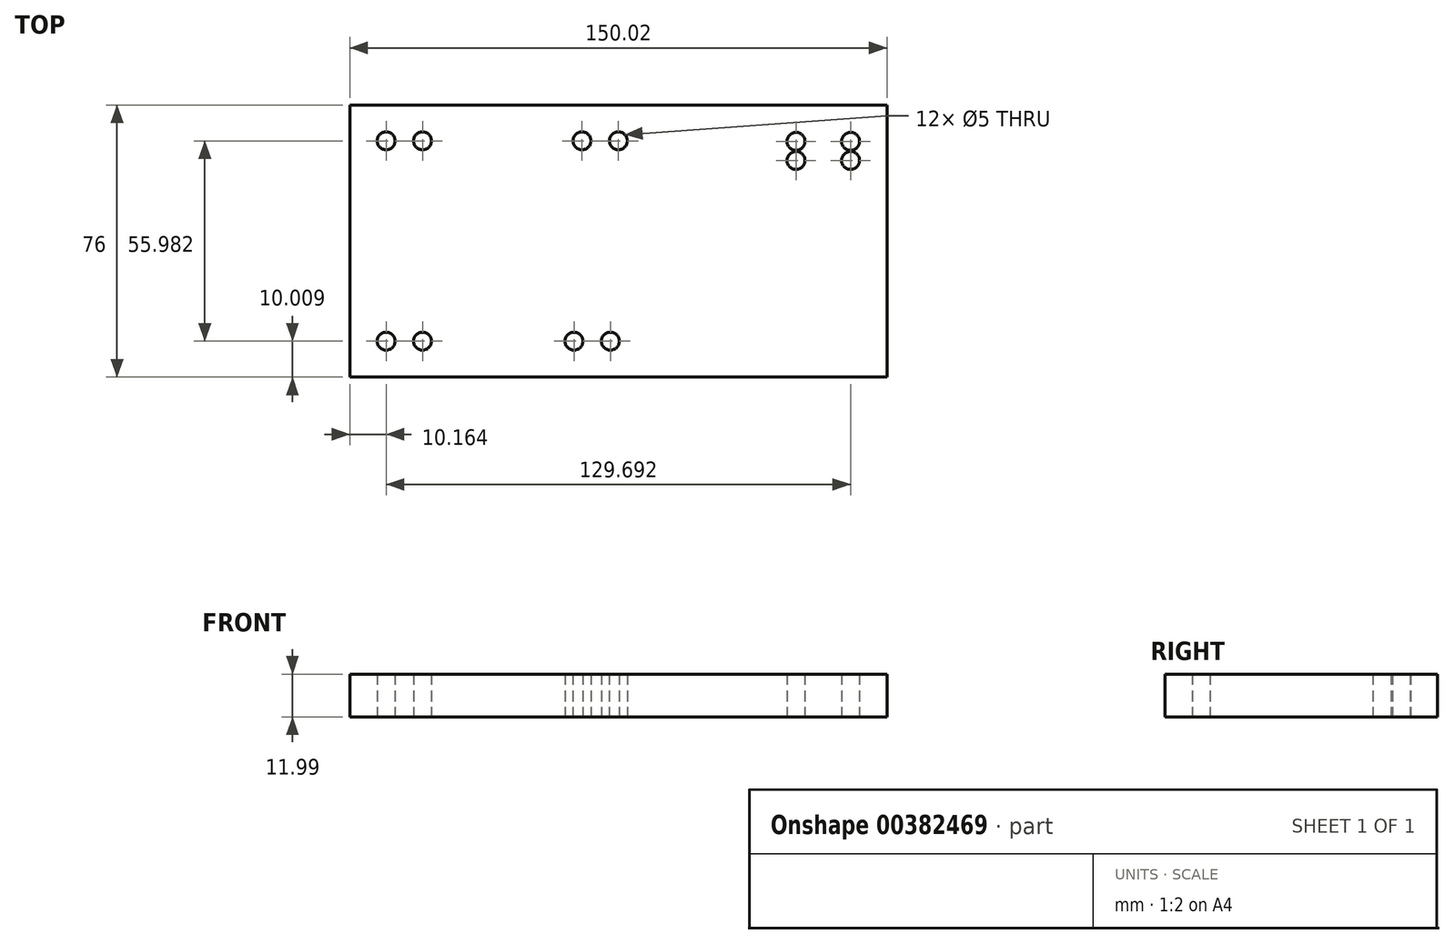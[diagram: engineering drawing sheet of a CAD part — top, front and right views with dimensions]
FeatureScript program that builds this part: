
annotation { "Feature Type Name" : "Feature", "Feature Type Description" : "" }
export const myFeature = defineFeature(function(context is Context, id is Id, definition is map)
    precondition{}
    {
        {
            var Q0;
            Q0=qCreatedBy(makeId("Top.planeOp"),FACE);
            var sketch = newSketch(context, id + "F0", { "sketchPlane" : qUnion([Q0])});
            skLineSegment(sketch, "E0.bottom", {"start": v(75, -38) * mm, "end": v(-75, -38) * mm});
            skLineSegment(sketch, "E0.top", {"start": v(75, 38) * mm, "end": v(-75, 38) * mm});
            skLineSegment(sketch, "E0.left", {"start": v(75, -38) * mm, "end": v(75, 38) * mm});
            skLineSegment(sketch, "E0.right", {"start": v(-75, -38) * mm, "end": v(-75, 38) * mm});
            skPoint(sketch, "E0.middle", {"position": v(0, 0) * mm});
            skCircle(sketch, "E1", {"center": v(-64.85, 28) * mm, "radius": 2.5 * mm});
            skCircle(sketch, "E2", {"center": v(-54.69, 28) * mm, "radius": 2.5 * mm});
            skCircle(sketch, "E3", {"center": v(-10.16, 28) * mm, "radius": 2.5 * mm});
            skCircle(sketch, "E4", {"center": v(0, 28) * mm, "radius": 2.5 * mm});
            skCircle(sketch, "E5", {"center": v(-2.24, -28) * mm, "radius": 2.5 * mm});
            skCircle(sketch, "E6", {"center": v(-12.4, -28) * mm, "radius": 2.5 * mm});
            skCircle(sketch, "E7", {"center": v(-64.85, -28) * mm, "radius": 2.5 * mm});
            skCircle(sketch, "E8", {"center": v(-54.69, -28) * mm, "radius": 2.5 * mm});
            skCircle(sketch, "E9", {"center": v(64.85, 27.84) * mm, "radius": 2.5 * mm});
            skCircle(sketch, "E10", {"center": v(49.6, 27.84) * mm, "radius": 2.5 * mm});
            skCircle(sketch, "E11", {"center": v(49.6, 22.5) * mm, "radius": 2.5 * mm});
            skCircle(sketch, "E12", {"center": v(64.85, 22.5) * mm, "radius": 2.5 * mm});
            skSolve(sketch);
        }
        {
            var Q0;
            Q0=makeQuery(id+"F0.imprint","IMPRINT",FACE,{"disambiguationData":[TD([[makeQuery(id+"F0.imprint","IMPRINT",EDGE,{"derivedFrom":sQuery(id+"F0.wireOp",EDGE,"E0.bottom")}),-1.0]])]});
            extrude(context, id + "F1", {"entities" : qUnion([Q0]), "depth" : 12 * mm});
        }
    });
